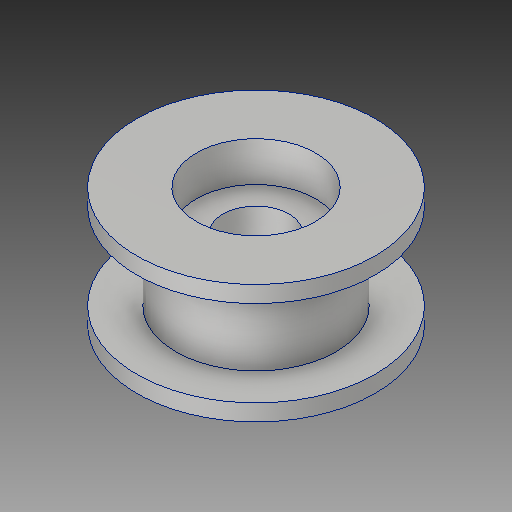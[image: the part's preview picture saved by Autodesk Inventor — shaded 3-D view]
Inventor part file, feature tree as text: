
AUTODESK INVENTOR PART (.ipt)
format: ipt  version: 2019 (Build 230136000, 136)  size: 153,600 bytes
history: native  units: mm
features: sketch x2, revolve x1, extrude x1, mirror x1
ambient origin geometry x8: Origin, YZ Plane, XZ Plane, XY Plane, X Axis, Y Axis, Z Axis, Center Point
bodies: Solid1 (feature_tree)
feature tree (5):
  revolve  "Revolution1"  [1 undecoded]
  extrude  "Extrusion1"  Depth=9.0mm
  mirror  "Mirror1"
  sketch  "Sketch1"  dims[d0=2.5mm d1=6.5mm]
  sketch  "Sketch2"  dims[d2=9.0mm d3=9.0mm d4=6.05mm d5=90.0deg d6=9.0mm d7=3.0mm d8=0.0mm]
note: 1 required parameter value undecoded (feature->parameter linkage not recoverable at this tier; creation-order binding heuristic only, values carry confidence <= 0.55)
